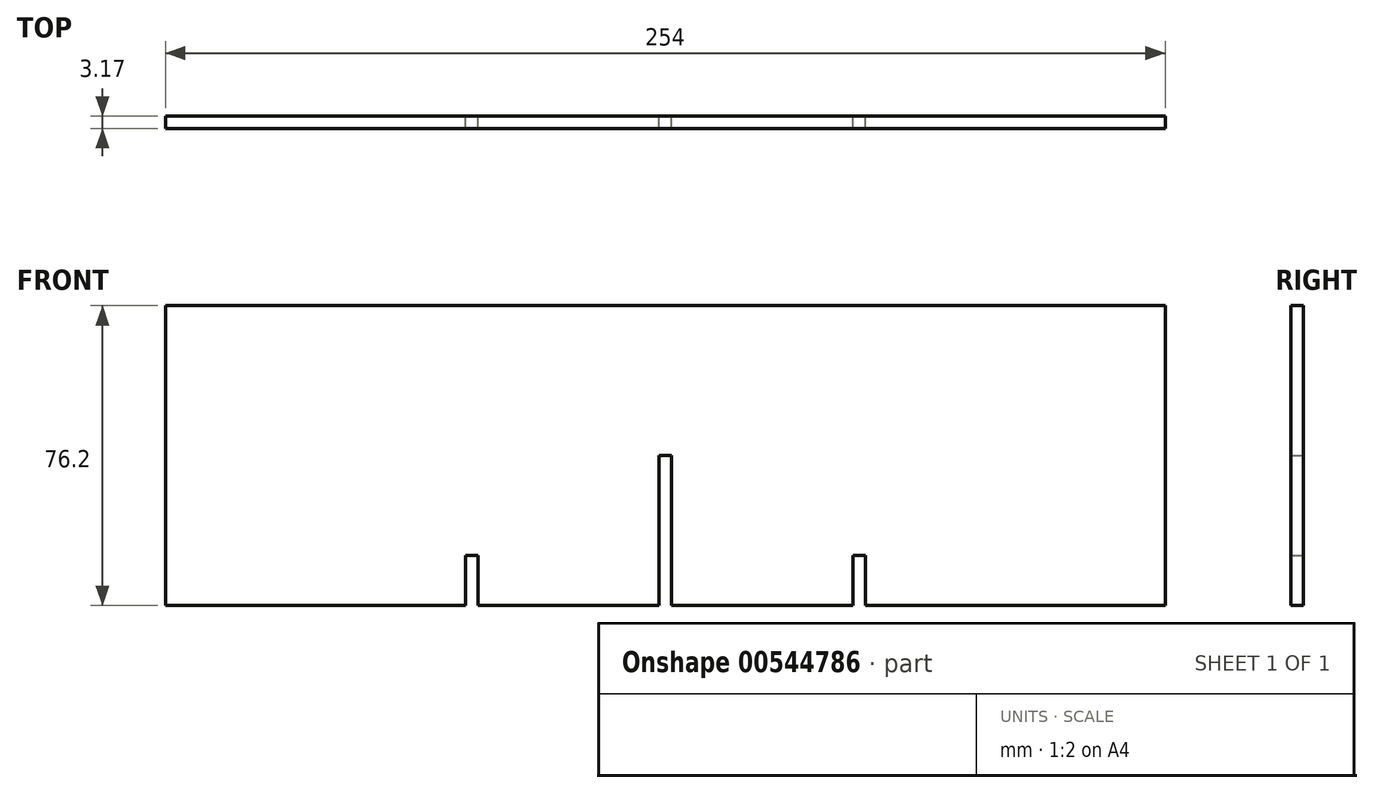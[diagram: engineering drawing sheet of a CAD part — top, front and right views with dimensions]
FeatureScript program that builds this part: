
annotation { "Feature Type Name" : "Feature", "Feature Type Description" : "" }
export const myFeature = defineFeature(function(context is Context, id is Id, definition is map)
    precondition{}
    {
        {
            var Q0;
            Q0=qCreatedBy(makeId("Front.planeOp"),FACE);
            var sketch = newSketch(context, id + "F0", { "sketchPlane" : qUnion([Q0])});
            skLineSegment(sketch, "E0.bottom", {"start": v(-127, 38.1) * mm, "end": v(127, 38.1) * mm});
            skLineSegment(sketch, "E0.top", {"start": v(-127, -38.1) * mm, "end": v(127, -38.1) * mm});
            skLineSegment(sketch, "E0.left", {"start": v(-127, 38.1) * mm, "end": v(-127, -38.1) * mm});
            skLineSegment(sketch, "E0.right", {"start": v(127, 38.1) * mm, "end": v(127, -38.1) * mm});
            skPoint(sketch, "E0.middle", {"position": v(0, 0) * mm});
            skLineSegment(sketch, "E1.top", {"start": v(-1.59, 0) * mm, "end": v(1.59, 0) * mm});
            skLineSegment(sketch, "E2.MirrorCS", {"start": v(1.59, -38.1) * mm, "end": v(1.59, 0) * mm});
            skLineSegment(sketch, "E3.MirrorCS", {"start": v(-1.59, -38.1) * mm, "end": v(-1.59, 0) * mm});
            skLineSegment(sketch, "E4.MirrorCS", {"start": v(-50.8, -25.4) * mm, "end": v(-47.62, -25.4) * mm});
            skLineSegment(sketch, "E5.MirrorCS", {"start": v(-47.63, -38.1) * mm, "end": v(-47.63, -25.4) * mm});
            skLineSegment(sketch, "E6.MirrorCS", {"start": v(-50.8, -38.1) * mm, "end": v(-50.8, -25.4) * mm});
            skLineSegment(sketch, "E7.MirrorCS", {"start": v(50.8, -25.4) * mm, "end": v(47.62, -25.4) * mm});
            skLineSegment(sketch, "E8.MirrorCS", {"start": v(47.63, -38.1) * mm, "end": v(47.63, -25.4) * mm});
            skLineSegment(sketch, "E9.MirrorCS", {"start": v(50.8, -38.1) * mm, "end": v(50.8, -25.4) * mm});
            skSolve(sketch);
        }
        {
            var Q0;
            {var subQ2=sQuery(id+"F0.wireOp",EDGE,"E0.left");Q0=makeQuery(id+"F0.imprint","IMPRINT",FACE,{"disambiguationData":[TD([[makeQuery(id+"F0.imprint","IMPRINT",EDGE,{"derivedFrom":subQ2}),1.0]])]});}
            extrude(context, id + "F1", {"entities" : qUnion([Q0]), "depth" : 3.17 * mm, "offsetDistance" : 25.4 * mm});
        }
    });
